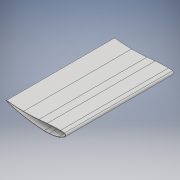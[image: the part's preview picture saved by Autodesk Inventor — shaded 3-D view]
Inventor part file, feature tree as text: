
AUTODESK INVENTOR PART (.ipt)
format: ipt  version: 2018.2 (Build 222227000, 227)  size: 136,192 bytes
history: native  units: mm
features: extrude x1, shell x1, sketch x1, projected_geometry x1
ambient origin geometry x8: Origin, YZ Plane, XZ Plane, XY Plane, X Axis, Y Axis, Z Axis, Center Point
bodies: Body1 (feature_tree)
feature tree (4):
  extrude  "押し出し1"  Depth=225.0mm TaperAngle=0.0deg
  shell  "シェル1"  Thickness=1.0mm
  sketch  "スケッチ1"
  projected_geometry  "投影ループ1"
